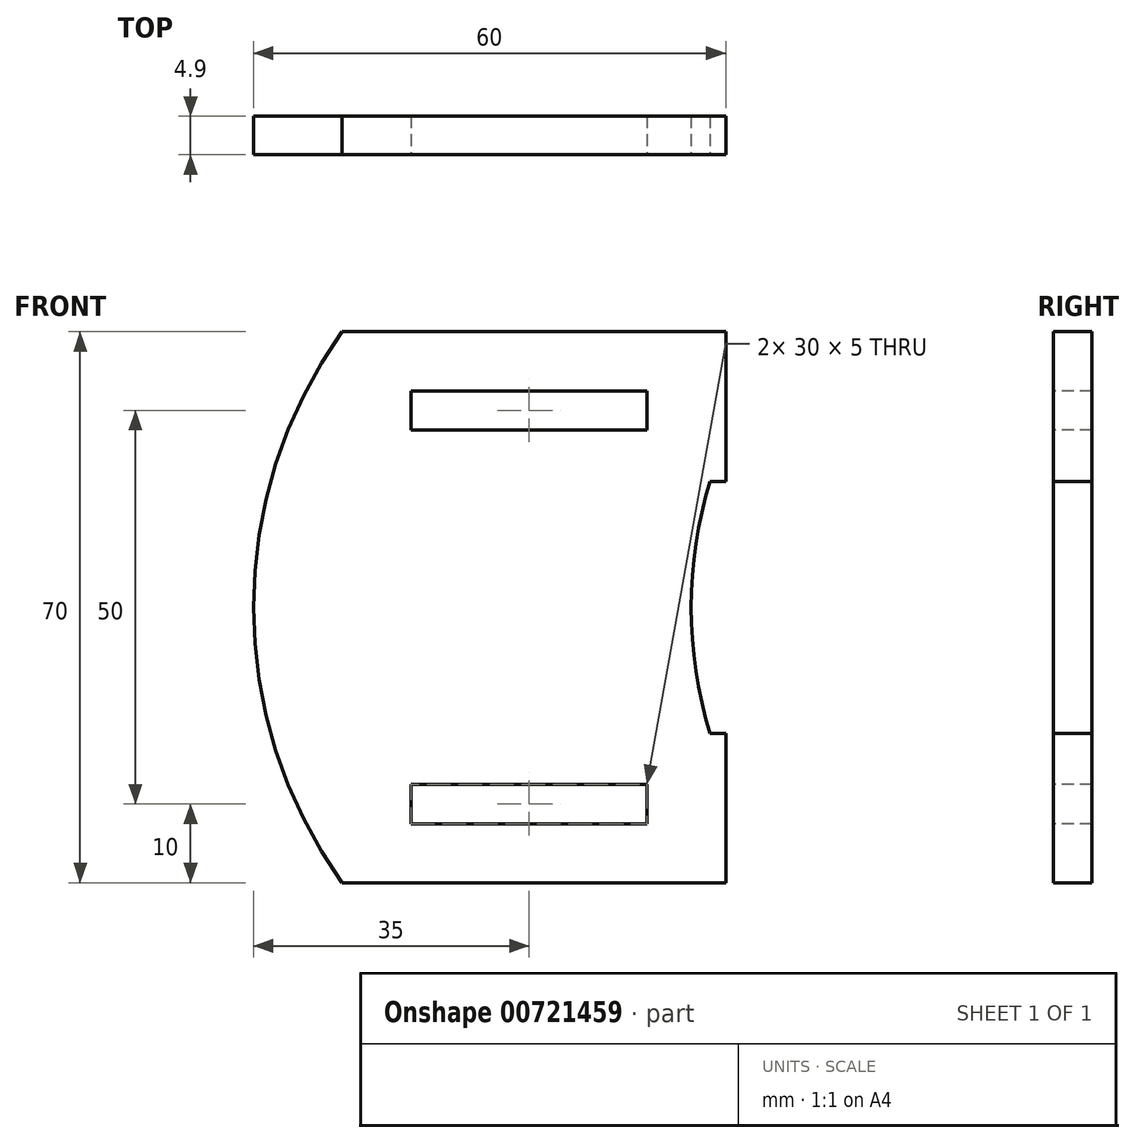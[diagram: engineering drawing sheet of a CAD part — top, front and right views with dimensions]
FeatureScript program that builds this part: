
annotation { "Feature Type Name" : "Feature", "Feature Type Description" : "" }
export const myFeature = defineFeature(function(context is Context, id is Id, definition is map)
    precondition{}
    {
        {
            var Q0;
            Q0=qCreatedBy(makeId("Front.planeOp"),FACE);
            var sketch = newSketch(context, id + "F0", { "sketchPlane" : qUnion([Q0])});
            skCircle(sketch, "E0", {"center": v(0, 0) * mm, "radius": 60 * mm});
            skSolve(sketch);
        }
        {
            var Q0;
            Q0=makeQuery(id+"F0.imprint","IMPRINT",FACE,{"disambiguationData":[TD([[makeQuery(id+"F0.imprint","IMPRINT",EDGE,{"derivedFrom":sQuery(id+"F0.wireOp",EDGE,"E0")}),1.0]])]});
            extrude(context, id + "F1", {"entities" : qUnion([Q0]), "depth" : 4.9 * mm, "offsetDistance" : 25.4 * mm});
        }
        {
            var Q0;
            Q0=makeQuery(id+"F1.opExtrude","CAP_FACE",FACE,{"disambiguationData":[OSD([sQuery(id+"F0.wireOp",EDGE,"E0")])],"isStart":false});
            var sketch = newSketch(context, id + "F2", { "sketchPlane" : qUnion([Q0])});
            skLineSegment(sketch, "E1.right", {"start": v(-60, 35) * mm, "end": v(-60, -35) * mm});
            skPoint(sketch, "E1.middle", {"position": v(0, 0) * mm});
            skLineSegment(sketch, "E2.bottom", {"start": v(-60, 35) * mm, "end": v(0, 35) * mm});
            skLineSegment(sketch, "E2.top", {"start": v(-60, -35) * mm, "end": v(0, -35) * mm});
            skLineSegment(sketch, "E2.right", {"start": v(0, 35) * mm, "end": v(0, -35) * mm});
            skSolve(sketch);
        }
        {
            var Q0;
            {var subQ0=sQuery(id+"F2.wireOp",EDGE,"E2.right");Q0=makeQuery(id+"F2.imprint","IMPRINT",FACE,{"disambiguationData":[TD([[makeQuery(id+"F2.imprint","IMPRINT",EDGE,{"derivedFrom":subQ0}),1.0]])]});}
            extrude(context, id + "F3", {"entities" : qUnion([Q0]), "operationType" : NewBodyOperationType.REMOVE, "endBound" : BoundingType.THROUGH_ALL, "oppositeDirection" : true, "depth" : 25.4 * mm, "offsetDistance" : 25.4 * mm});
        }
        {
            var Q0;
            Q0=makeQuery(id+"F1.opExtrude","CAP_FACE",FACE,{"disambiguationData":[OSD([sQuery(id+"F0.wireOp",EDGE,"E0")])],"isStart":false});
            var sketch = newSketch(context, id + "F4", { "sketchPlane" : qUnion([Q0])});
            skLineSegment(sketch, "E3.bottom", {"start": v(0, 16) * mm, "end": v(0, 16) * mm});
            skLineSegment(sketch, "E3.top", {"start": v(0, -16) * mm, "end": v(0, -16) * mm});
            skLineSegment(sketch, "E3.left", {"start": v(0, 16) * mm, "end": v(0, -16) * mm});
            skLineSegment(sketch, "E3.right", {"start": v(0, 16) * mm, "end": v(0, -16) * mm});
            skPoint(sketch, "E3.middle", {"position": v(0, 0) * mm});
            skFitSpline(sketch, "E4", {"points": [v(0, 16) * mm, v(0, -16) * mm], "startDerivative": vector(0, -30) * mm, "endDerivative": vector(0, -30) * mm});
            skLineSegment(sketch, "E5.left", {"start": v(0, -16) * mm, "end": v(0, 16) * mm});
            skLineSegment(sketch, "E5.right", {"start": v(0, -16) * mm, "end": v(0, 16) * mm});
            skLineSegment(sketch, "E6.bottom", {"start": v(0, -16) * mm, "end": v(-2, -16) * mm});
            skLineSegment(sketch, "E6.top", {"start": v(0, 16) * mm, "end": v(-2, 16) * mm});
            skLineSegment(sketch, "E6.right", {"start": v(-2, -16) * mm, "end": v(-2, 16) * mm});
            skArc(sketch, "E7", {"start": v(-2, 16) * mm, "mid": v(-4.4, 0) * mm, "end": v(-2, -16) * mm});
            skSolve(sketch);
        }
        {
            var Q0;
            Q0=makeQuery(id+"F4.imprint","IMPRINT",FACE,{"disambiguationData":[TD([[makeQuery(id+"F4.imprint","IMPRINT",EDGE,{"derivedFrom":sQuery(id+"F4.wireOp",EDGE,"E6.right")}),1.0]])]});
            var Q1;
            Q1=makeQuery(id+"F4.imprint","IMPRINT",FACE,{"disambiguationData":[TD([[makeQuery(id+"F4.imprint","IMPRINT",EDGE,{"derivedFrom":sQuery(id+"F4.wireOp",EDGE,"E6.bottom")}),-1.0]])]});
            extrude(context, id + "F5", {"entities" : qUnion([Q0, Q1]), "operationType" : NewBodyOperationType.REMOVE, "endBound" : BoundingType.THROUGH_ALL, "oppositeDirection" : true, "depth" : 25.4 * mm, "offsetDistance" : 25.4 * mm});
        }
        {
            var Q0;
            Q0=makeQuery(id+"F1.opExtrude","CAP_FACE",FACE,{"disambiguationData":[OSD([sQuery(id+"F0.wireOp",EDGE,"E0")])],"isStart":false});
            var sketch = newSketch(context, id + "F6", { "sketchPlane" : qUnion([Q0])});
            skPoint(sketch, "E8.middle", {"position": v(0, 0) * mm});
            skLineSegment(sketch, "E9.bottom", {"start": v(-10, 27.5) * mm, "end": v(-40, 27.5) * mm});
            skLineSegment(sketch, "E9.top", {"start": v(-10, 22.5) * mm, "end": v(-40, 22.5) * mm});
            skLineSegment(sketch, "E9.left", {"start": v(-10, 27.5) * mm, "end": v(-10, 22.5) * mm});
            skLineSegment(sketch, "E9.right", {"start": v(-40, 27.5) * mm, "end": v(-40, 22.5) * mm});
            skPoint(sketch, "E9.middle", {"position": v(-25, 25) * mm});
            skLineSegment(sketch, "E10.bottom", {"start": v(-10, -22.5) * mm, "end": v(-40, -22.5) * mm});
            skLineSegment(sketch, "E10.top", {"start": v(-10, -27.5) * mm, "end": v(-40, -27.5) * mm});
            skLineSegment(sketch, "E10.left", {"start": v(-10, -22.5) * mm, "end": v(-10, -27.5) * mm});
            skLineSegment(sketch, "E10.right", {"start": v(-40, -22.5) * mm, "end": v(-40, -27.5) * mm});
            skPoint(sketch, "E10.middle", {"position": v(-25, -25) * mm});
            skSolve(sketch);
        }
        {
            var Q0;
            {var subQ5=sQuery(id+"F6.wireOp",EDGE,"E9.bottom");Q0=makeQuery(id+"F6.imprint","IMPRINT",FACE,{"disambiguationData":[TD([[makeQuery(id+"F6.imprint","IMPRINT",EDGE,{"derivedFrom":subQ5}),1.0]])]});}
            var Q1;
            {var subQ5=sQuery(id+"F6.wireOp",EDGE,"E9.top");Q1=makeQuery(id+"F6.imprint","IMPRINT",FACE,{"disambiguationData":[TD([[makeQuery(id+"F6.imprint","IMPRINT",EDGE,{"derivedFrom":subQ5}),-1.0]])]});}
            var Q2;
            {var subQ5=sQuery(id+"F6.wireOp",EDGE,"E10.bottom");Q2=makeQuery(id+"F6.imprint","IMPRINT",FACE,{"disambiguationData":[TD([[makeQuery(id+"F6.imprint","IMPRINT",EDGE,{"derivedFrom":subQ5}),1.0]])]});}
            var Q3;
            {var subQ5=sQuery(id+"F6.wireOp",EDGE,"E10.top");Q3=makeQuery(id+"F6.imprint","IMPRINT",FACE,{"disambiguationData":[TD([[makeQuery(id+"F6.imprint","IMPRINT",EDGE,{"derivedFrom":subQ5}),-1.0]])]});}
            extrude(context, id + "F7", {"entities" : qUnion([Q0, Q1, Q2, Q3]), "operationType" : NewBodyOperationType.REMOVE, "endBound" : BoundingType.THROUGH_ALL, "oppositeDirection" : true, "depth" : 25.4 * mm, "offsetDistance" : 25.4 * mm});
        }
    });
